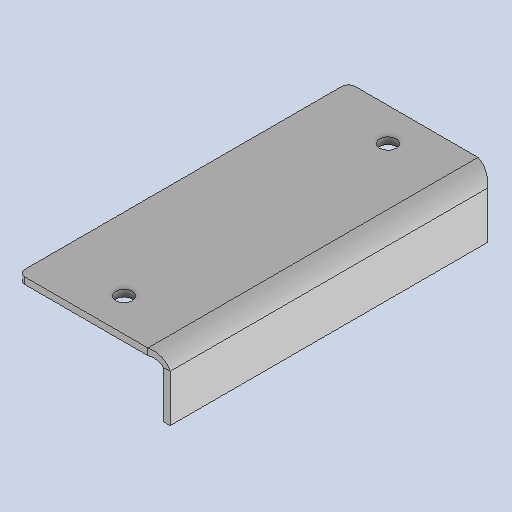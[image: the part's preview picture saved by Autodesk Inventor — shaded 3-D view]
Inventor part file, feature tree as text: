
AUTODESK INVENTOR PART (.ipt)
format: ipt  version: 2025 (Build 290162010, 162A)  size: 203,264 bytes
history: native  units: mm
features: sheet_metal_op x4, sketch x3, other x3, extrude x1, fillet x1, projected_geometry x1
ambient origin geometry x8: Origin, YZ Plane, XZ Plane, XY Plane, X Axis, Y Axis, Z Axis, Center Point
bodies: Solid1 (feature_tree)
feature tree (13):
  sheet_metal_op  "Face1"
  extrude  "Extrusion3"  Depth=100.0mm
  fillet  "Fillet2"  Radius=2.0mm
  sheet_metal_op  "Flange2"
  sketch  "Sketch1"  dims[d0=44.0mm d1=100.0mm d2=2.0mm]
  other  "Plate1"
  sketch  "Sketch8"  dims[d34=5.0mm]
  projected_geometry  "Projected Loop3"
  sketch  "Sketch9"  dims[d35=10.0mm d36=0.0mm d37=0.0mm d38=2.0mm d39=2.0mm d40=1.0mm d41=4.0mm d42=2.75mm d43=19.0mm d44=90.0deg d45=2.75mm d46=8.0mm d47=2.0mm d48=2.75mm]
  other  "Plate3"
  sheet_metal_op  "Bend2"
  sheet_metal_op  "Corner2"
  other  "Definition1"
